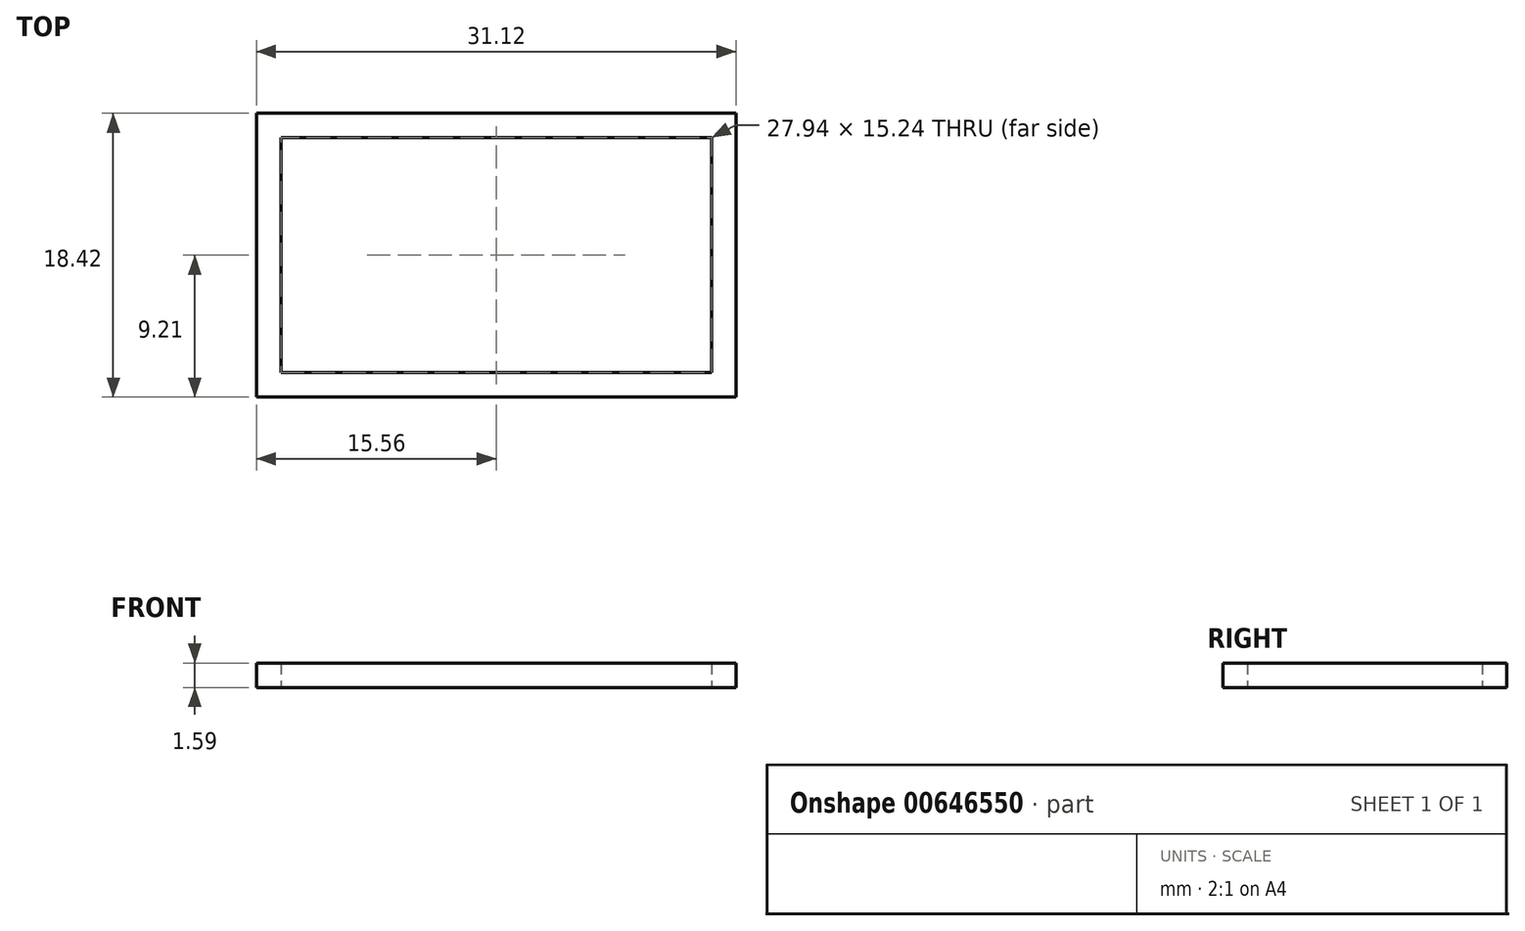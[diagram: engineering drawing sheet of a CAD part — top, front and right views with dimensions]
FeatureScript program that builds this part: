
annotation { "Feature Type Name" : "Feature", "Feature Type Description" : "" }
export const myFeature = defineFeature(function(context is Context, id is Id, definition is map)
    precondition{}
    {
        {
            var Q0;
            Q0=qCreatedBy(makeId("Top.planeOp"),FACE);
            var sketch = newSketch(context, id + "F0", { "sketchPlane" : qUnion([Q0])});
            skLineSegment(sketch, "E0.bottom", {"start": v(13.97, 7.62) * mm, "end": v(-13.97, 7.62) * mm});
            skLineSegment(sketch, "E0.top", {"start": v(13.97, -7.62) * mm, "end": v(-13.97, -7.62) * mm});
            skLineSegment(sketch, "E0.left", {"start": v(13.97, 7.62) * mm, "end": v(13.97, -7.62) * mm});
            skLineSegment(sketch, "E0.right", {"start": v(-13.97, 7.62) * mm, "end": v(-13.97, -7.62) * mm});
            skPoint(sketch, "E0.middle", {"position": v(0, 0) * mm});
            skLineSegment(sketch, "E1.bottom", {"start": v(15.56, 9.2) * mm, "end": v(-15.56, 9.2) * mm});
            skLineSegment(sketch, "E1.top", {"start": v(15.56, -9.2) * mm, "end": v(-15.56, -9.2) * mm});
            skLineSegment(sketch, "E1.left", {"start": v(15.56, 9.2) * mm, "end": v(15.56, -9.2) * mm});
            skLineSegment(sketch, "E1.right", {"start": v(-15.56, 9.2) * mm, "end": v(-15.56, -9.2) * mm});
            skSolve(sketch);
        }
        {
            var Q0;
            Q0 = qSketchRegion(id + "F0", true);
            extrude(context, id + "F1", {"entities" : qUnion([Q0]), "depth" : 1.59 * mm, "offsetDistance" : 25.4 * mm});
        }
    });
